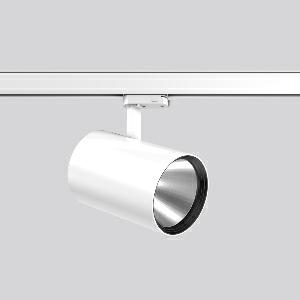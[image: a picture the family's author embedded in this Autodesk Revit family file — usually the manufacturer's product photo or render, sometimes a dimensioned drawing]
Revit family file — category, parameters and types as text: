
# Revit family: deecos_s_maxi_742223_002_76_5d8e
name_source: partatom
category: Lighting Fixtures
units: mm (PartAtom-declared; Revit-internal decimal feet)

## family parameters
Cut with Voids When Loaded = No
Host = Face
Light Source = No
Part Type = Normal
Room Calculation Point = No
Round Connector Dimension = Use Diameter
Shared = No

## types (1)
- DEECOS S maxi (1 x LED Modul 930, 4150 lm, 3000)
    Apparent Load = 35 VA
    Approval mark = CE
    CIE Flux Codes = 97 100 100 100 100
    Color Rendering = 90
    Color Temperature = 3000
    Default Elevation = 1800 mm
    Description = Series: DEECOS S maxi
LED surface-mounted projector in modern design with no visible cooling ribs. Housing: die-cast aluminium, powder-coated. Rotation range: 356°. Swivel range: 90°. Black plastic ring and recessed LED to prevent glare from the side. Optical assembly with reflector made of MIRO-Silver with 98% total light reflection for outstanding efficiency - can be changed without tools. Best colour rendering index Ra>90. With adapter for RZB 3-circuit DALI tracks. Suitable for Track on ceiling, Wall track. High quality converter without flickering and stroboscopic effect. The following accessories can be mounted without use of tools: interchangeable lenses, decorative glasses, honeycomb louvre, clear and frosted diffusers, white interchangeable plastic ring. 
Colour: traffic white, matt (RAL 9016)
Diameter: 123 mm
Height: 200 mm
Lamp: LED
Socket: without socket
Colour temperature: 3000K
Colour rendering index (CRI): 92
System power: 35 W
Rated luminous flux: 4150 lm
Luminous efficiency: 119 lm/W
Control gear: Converter, dimmable, DALI
Protection class: I
Type of protection: IP 20
    Height = 200 mm  [stored 0.656168 ft]
    Lamp = 1 x LED Modul 930
    Lamp Light Flux = 4150 lm
    Lamp count = 1
    Length = 123 mm
    Lifetime = 50000 h
    Luminous efficacy = 119 lm/W
    Manufacturer = RZB
    ModVariant = No
    Model = 742223.002.76
    Mounting Place = Ceiling
    Mounting Type = Rail mounted
    Number of Poles = 1
    OnlyDefault = Yes
    Power Factor = 1
    Product Name = DEECOS S maxi
    Product group = Track mounted projectors
    ProductGroupID = 301
    Protection Class = Protection class I
    Protection Degree = IP 20
    RLX_Detail_Level = 1
    RLX_Emergency_Light_Flux = 0 lm
    RLX_Emergency_Type = 0
    RLX_Emergency_Type_DB = No
    RlxData = <blob elided: 38625 chars, md5=1beb81a0>
    Socket = socket
    Standby Power = 0 W
    System Light Flux = 4150 lm
    System Power = 35 W
    Type Comments = Product without accessories
    Type Image = 741954.002.jpg
    URL = http://relux.com
    VarID = ---
    Voltage = 230 V
    Voltage Range = 220-240 V
    Weight = 0.00 kg
    Width = 0 mm  [stored 0 ft]

note: [stored X ft] marks values corroborated as IEEE doubles in the binary element streams (Revit-internal decimal feet)

## geometry (parser evidence)
native form markers: Blend x4, Sweep x12
no freeform markers — native parametric forms only
